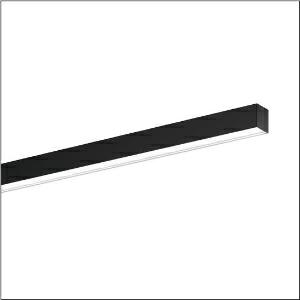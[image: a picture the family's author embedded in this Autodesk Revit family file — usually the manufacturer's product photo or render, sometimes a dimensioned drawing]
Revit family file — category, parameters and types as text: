
# Revit family: silica_r__21_51mx20db32bb_e5b9
name_source: partatom
category: Lighting Fixtures
units: mm (PartAtom-declared; Revit-internal decimal feet)

## family parameters
Cut with Voids When Loaded = No
Host = Face
Light Source = No
Part Type = Normal
Room Calculation Point = No
Round Connector Dimension = Use Diameter
Shared = No

## types (1)
- --- (1 x LED, 3000 lm, 20.2 W, 3000K)
    Apparent Load = 20 VA
    CIE Flux Codes = 48 79 96 100 100
    Color Rendering = 80
    Color Temperature = 3000K
    Default Elevation = 1800 mm
    Description = Silica® 21, office luminaire, primary optical cover: cover, of PMMA, opal, light emission: direct distribution, primary light characteristic: symmetric, installation type: surface-mounted, LED, rated luminous flux: 3.000lm, luminous efficacy: 149lm/W, light colour: 830, colour temperature: 3000K, with terminal, 3+2-pole, max. 2.5mm², mains connection: 220..240V, AC, 50/60Hz, luminaire housing, of aluminium, jet black (RAL 9005), length: 1.504mm, width: 53mm, height: 53mm, protection rating (complete): IP20, insulation class (complete): insulation class I (protective earthing), certification: CE, permissible operating ambient temperature: 0..+35°C, standard: EN 50419, packaging unit: 1 piece
    Height = 0 mm  [stored 0 ft]
    Lamp = 1 x LED
    Lamp Light Flux = 3000 lm
    Lamp Power = 20.2 W
    Lamp count = 1
    Length = 1504 mm
    Luminous efficacy = 149 lm/W
    Manufacturer = Siteco
    ModVariant = No
    Model = 51MX20DB32BB
    Mounting Place = Ceiling
    Mounting Type = Recessed
    Number of Poles = 1
    OnlyDefault = Yes
    Power Factor = 1
    Product Name = Silica® 21
    Product group = office luminaire | ceiling recessed
    ProductGroupID = 401
    Protection Class = Protection class I
    Protection Degree = IP 20
    RLX_Detail_Level = 1
    RLX_Emergency_Light_Flux = 0 lm
    RLX_Emergency_Type = 0
    RLX_Emergency_Type_DB = No
    RlxData = <blob elided: 28521 chars, md5=c38841fa>
    Socket = socket
    Standby Power = 0 W
    System Light Flux = 3000 lm
    System Power = 20 W
    Type Comments = factory setting: luminous flux: 100 % | dim-lin: 254 | 233 mA
    Type Image = l_1313584.jpg
    URL = http://relux.com
    VarID = @adj_066407
    Voltage = 0 V
    Weight = 0.00 kg
    Width = 53 mm

note: [stored X ft] marks values corroborated as IEEE doubles in the binary element streams (Revit-internal decimal feet)

## geometry (parser evidence)
native form markers: Blend x4, Sweep x10
no freeform markers — native parametric forms only
